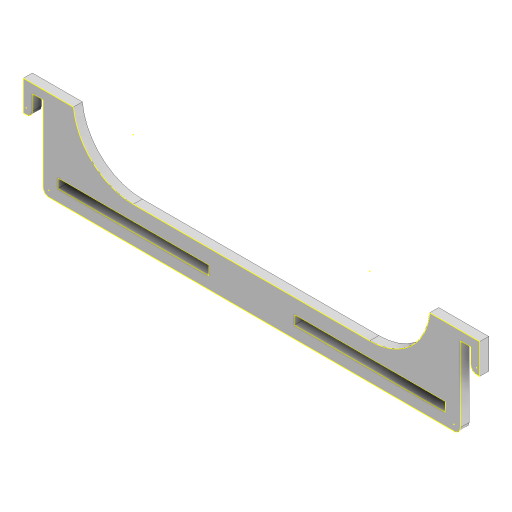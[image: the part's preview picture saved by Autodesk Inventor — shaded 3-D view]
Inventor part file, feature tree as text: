
AUTODESK INVENTOR PART (.ipt)
format: ipt  version: 2023 (Build 270158000, 158)  size: 169,984 bytes
history: native  units: mm
features: sketch x3, extrude x2, projected_geometry x1
ambient origin geometry x8: Origin, YZ Plane, XZ Plane, XY Plane, X Axis, Y Axis, Z Axis, Center Point
bodies: Solid1 (feature_tree)
feature tree (6):
  extrude  "Extrusion1"  Depth=30.0mm
  extrude  "Extrusion2"  Depth=3.0mm
  sketch  "Sketch3"  dims[d4=3.0mm d5=10.0mm d6=3.5mm d7=3.0mm d8=3.0mm d9=10.0mm d10=2.0mm d11=3.0mm d12=20.0mm d13=5.0mm d14=50.0mm d15=3.0mm d16=5.0mm d17=50.0mm d18=2.0mm d19=3.0mm d20=0.0mm d21=5.0mm d22=10.0mm d23=10.0mm d24=20.0mm d25=10.0mm d26=0.0mm]
  sketch  "Sketch1"  dims[d0=138.5mm d1=30.0mm]
  sketch  "Sketch2"  dims[d2=3.5mm d3=3.0mm]
  projected_geometry  "Projected Loop1"
